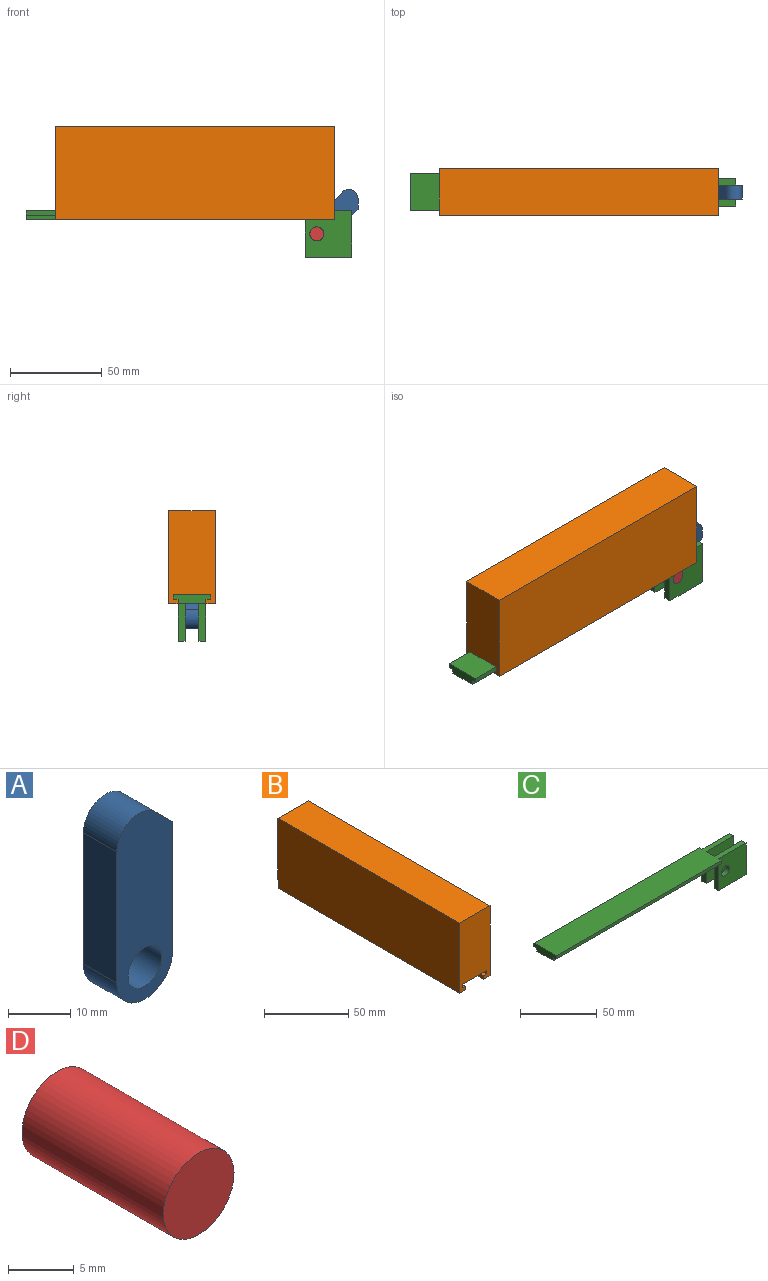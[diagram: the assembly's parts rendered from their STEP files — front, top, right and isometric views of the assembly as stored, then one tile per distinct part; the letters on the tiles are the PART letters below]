
ASSEMBLY  parts=4 mates=3
PART A: 8 faces, bbox 12.7x7.6x37.3 mm
  f0: plane 7.62x4.03mm, normal (0.71,0,0.71), area 43.4mm2, adj f3,f5,f6,f7
  f1: plane 25.84x7.62mm, normal (-1,0,0), area 196.9mm2, adj f2,f5,f6,f7
  f2: cylinder r=6.35mm len=12.7mm, axis (0,1,0), area 152mm2, adj f1,f3,f5,f6
  f3: plane 25.4x7.62mm, normal (1,0,0), area 193.5mm2, adj f0,f2,f5,f6
  f4: cylinder r=3.81mm len=7.62mm, axis (0,1,0), area 182.4mm2, adj f5,f6
  f5: plane 37.27x12.7mm, normal (0,-1,0), area 389.1mm2, adj f0,f1,f2,f3,f4,f7
  f6: plane 37.27x12.7mm, normal (0,1,0), area 389.1mm2, adj f0,f1,f2,f3,f4,f7
  f7: cylinder r=5.08mm len=8.67mm, axis (0,1,0), area 91.2mm2, adj f0,f1,f5,f6
PART B: 14 faces, bbox 25.4x152.4x50.8 mm
  f0: plane 152.4x5.08mm, normal (0,0,-1), area 774.2mm2, adj f1,f2,f3,f8
  f1: plane 50.8x25.4mm, normal (0,1,0), area 1200mm2, adj f0,f3,f4,f5,f6,f7,f8,f9
  f2: plane 50.8x25.4mm, normal (0,-1,0), area 1200mm2, adj f0,f3,f4,f5,f6,f7,f8,f9
  f3: plane 152.4x50.8mm, normal (-1,0,0), area 7741.9mm2, adj f0,f1,f2,f6
  f4: plane 152.4x5.08mm, normal (0,0,-1), area 774.2mm2, adj f1,f2,f5,f9
  f5: plane 152.4x50.8mm, normal (1,0,0), area 7741.9mm2, adj f1,f2,f4,f6
  f6: plane 152.4x25.4mm, normal (0,0,1), area 3871mm2, adj f1,f2,f3,f5
  f7: plane 152.4x2.54mm, normal (0,0,1), area 387.1mm2, adj f1,f2,f8,f13
  f8: plane 152.4x2.54mm, normal (1,0,0), area 387.1mm2, adj f0,f1,f2,f7
  f9: plane 152.4x2.54mm, normal (-1,0,0), area 387.1mm2, adj f1,f2,f4,f10
  f10: plane 152.4x2.54mm, normal (0,0,1), area 387.1mm2, adj f1,f2,f9,f11
  f11: plane 152.4x2.54mm, normal (-1,0,0), area 387.1mm2, adj f1,f2,f10,f12
  f12: plane 152.4x20.32mm, normal (0,0,-1), area 3096.8mm2, adj f1,f2,f11,f13
  f13: plane 152.4x2.54mm, normal (1,0,0), area 387.1mm2, adj f1,f2,f7,f12
PART C: 22 faces, bbox 177.8x20.3x25.4 mm
  f0: plane 25.4x3.81mm, normal (1,0,0), area 96.8mm2, adj f2,f8,f11,f19
  f1: plane 20.32x3.81mm, normal (-1,0,0), area 77.4mm2, adj f2,f3,f11,f19
  f2: plane 25.4x3.81mm, normal (0,0,-1), area 96.8mm2, adj f0,f1,f11,f19
  f3: plane 152.4x15.24mm, normal (0,0,-1), area 2322.6mm2, adj f1,f5,f11,f13,f15,f18
  f4: plane 2.54x2.54mm, normal (1,0,0), area 6.5mm2, adj f5,f6,f7,f8
  f5: plane 177.8x25.4mm, normal (0,1,0), area 986.7mm2, adj f3,f4,f6,f8,f13,f14,f15,f16
  f6: plane 152.4x2.54mm, normal (0,0,-1), area 387.1mm2, adj f4,f5,f7,f13
  f7: plane 152.4x2.54mm, normal (0,1,0), area 387.1mm2, adj f4,f6,f8,f13
  f8: plane 177.8x20.32mm, normal (0,0,1), area 3290.3mm2, adj f0,f4,f5,f7,f9,f11,f12,f13
  f9: plane 152.4x2.54mm, normal (0,-1,0), area 387.1mm2, adj f8,f10,f12,f13
  f10: plane 152.4x2.54mm, normal (0,0,-1), area 387.1mm2, adj f9,f11,f12,f13
  f11: plane 177.8x25.4mm, normal (0,-1,0), area 986.7mm2, adj f0,f1,f2,f3,f8,f10,f12,f13
  f12: plane 2.54x2.54mm, normal (1,0,0), area 6.5mm2, adj f8,f9,f10,f11
  f13: plane 20.32x5.08mm, normal (-1,0,0), area 90.3mm2, adj f3,f5,f6,f7,f8,f9,f10,f11
  f14: plane 25.4x3.81mm, normal (1,0,0), area 96.8mm2, adj f5,f8,f16,f17
  f15: plane 20.32x3.81mm, normal (-1,0,0), area 77.4mm2, adj f3,f5,f16,f17
  f16: plane 25.4x3.81mm, normal (0,0,-1), area 96.8mm2, adj f5,f14,f15,f17
  f17: plane 25.4x25.4mm, normal (0,-1,0), area 599.6mm2, adj f8,f14,f15,f16,f18,f21
  f18: plane 7.62x5.08mm, normal (1,0,0), area 38.7mm2, adj f3,f8,f17,f19
  f19: plane 25.4x25.4mm, normal (0,1,0), area 599.6mm2, adj f0,f1,f2,f8,f18,f20
  f20: cylinder r=3.81mm len=7.62mm, axis (0,-1,0), area 91.2mm2, adj f11,f19
  f21: cylinder r=3.81mm len=7.62mm, axis (0,-1,0), area 91.2mm2, adj f5,f17
PART D: 3 faces, bbox 7.6x15.2x7.6 mm
  f0: cylinder r=3.81mm len=15.24mm, axis (0,1,0), area 364.8mm2, adj f1,f2
  f1: plane 7.62x7.62mm, normal (0,-1,0), area 45.6mm2, adj f0
  f2: plane 7.62x7.62mm, normal (0,1,0), area 45.6mm2, adj f0
PLACE A rot(axis=(0,1,0),45deg) t=(166.18,47.83,-16.55)mm
PLACE B rot(axis=(0,0,1),90deg) t=(175.7,31.32,-8.93)mm
PLACE C t=(7.43,44.02,-5.12)mm fixed
PLACE D rot(axis=(0,1,0),45deg) t=(166.18,51.64,-16.55)mm
MATE fastened A.f4 <-> D.f0  axis (0,1,0) through (166.18,44.02,-16.55)mm
MATE slider B.f1 <-> C.f13  axis (-1,0,0) through (23.3,44.02,-3.85)mm
MATE revolute D.f0 <-> C.f20  axis (0,-1,0) through (166.18,36.4,-16.55)mm
